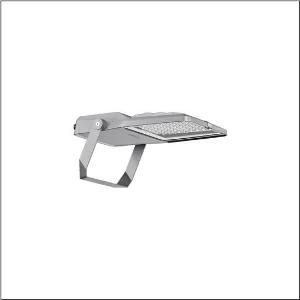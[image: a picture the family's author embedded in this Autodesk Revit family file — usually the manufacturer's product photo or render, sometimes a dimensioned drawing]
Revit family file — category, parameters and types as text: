
# Revit family: floodlight_fl_21_iq_mini___pl64_5xa7771d4e1a_9fb1
name_source: partatom
category: Lighting Fixtures
units: mm (PartAtom-declared; Revit-internal decimal feet)

## family parameters
Cut with Voids When Loaded = No
Host = Face
Light Source = No
Part Type = Normal
Room Calculation Point = No
Round Connector Dimension = Use Diameter
Shared = No

## types (1)
- --- (1 x LED, 17970 lm, 143 W, 4000K)
    Apparent Load = 143 VA
    CIE Flux Codes = 28 80 98 100 100
    Color Rendering = 70
    Color Temperature = 4000K
    Default Elevation = 1800 mm
    Description = Floodlight FL 21 iQ mini, floodlight, primary light control with lens, of PMMA, primary optical cover: protective disc, of toughened safety glass, transparent, light distribution: PL64, light emission: direct distribution, installation type: surface-mounted, LED, High Power LED, rated luminous flux: 17.970lm, luminous efficacy: 126lm/W, light colour: 740, colour temperature: 4000K, control: Auto-Match, Temp-Guard, Lumen-Switch, Night-Set, Smart-Wire, Light-Fading, Desk-Remote (wireless, voltage-free reading and setting of iQ features in the workshop via application-optimized NFC function/RFID function), optimised constant luminous flux control (CLO 2.0), with terminal, 6-pole, mains connection: 220..240V, AC, 50/60Hz, start of lifetime: 143W, end of service life: 152W, reduction: 61W, luminaire housing, of diecast aluminium, powder-coated, Siteco® metallic grey (DB 702S), corrosivity category C5 mid according to DIN EN ISO 12944, sealing non-destructively replaceable, mounting bracket, of steel, galvanised, powder-coated, Siteco® metallic grey (DB 702S), protection rating (complete): IP66, insulation class (complete): insulation class II (safety insulation), certification: CE, ENEC, VDE, protection symbol: D, impact resistance: IK08, permissible operating ambient temperature: -40..+40°C, permissible operating ambient temperature for outdoor applications: -40..+50°C, standard: DIN EN 12944, LABS conformity tested according to VDMA 24364:2018-05, packaging unit: 1 piece

Light Distribution: PL64
    Height = 70 mm
    Lamp = 1 x LED
    Lamp Light Flux = 17970 lm
    Lamp Power = 143 W
    Lamp count = 1
    Length = 485 mm
    Luminous efficacy = 126 lm/W
    Manufacturer = Siteco
    ModVariant = No
    Model = 5XA7771D4E1A
    Number of Poles = 1
    OnlyDefault = Yes
    Power Factor = 1
    Product Name = Floodlight FL 21 iQ mini | PL64
    Product group = floodlight | pylon annexe
    ProductGroupID = 6200
    Protection Class = Protection class II
    Protection Degree = IP 66
    RLX_Detail_Level = 1
    RLX_Emergency_Light_Flux = 0 lm
    RLX_Emergency_Type = 0
    RLX_Emergency_Type_DB = No
    RlxData = <blob elided: 96409 chars, md5=2385f2f7>
    Socket = socket
    Standby Power = 0 W
    System Light Flux = 17970 lm
    System Power = 143 W
    Type Comments = factory setting: luminous flux: 100 % | dim-lin: 254 | 730 mA
    Type Image = l_1006845.jpg
    URL = http://relux.com
    VarID = @adj_098329
    Voltage = 0 V
    Weight = 0.00 kg
    Width = 337 mm

## geometry (parser evidence)
native form markers: Blend x4, Sweep x13
no freeform markers — native parametric forms only
